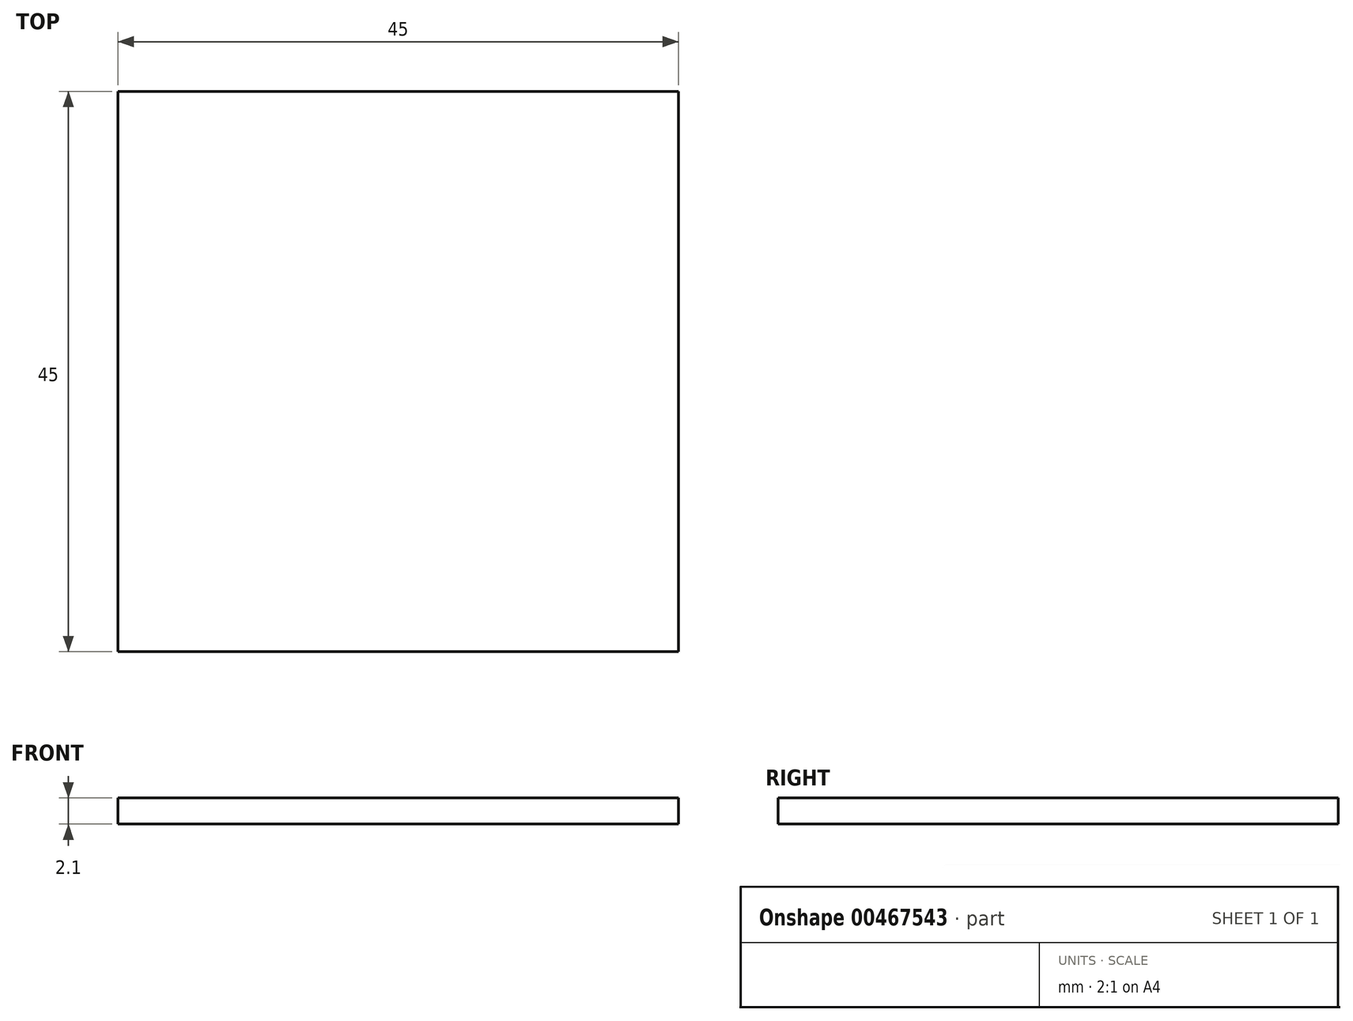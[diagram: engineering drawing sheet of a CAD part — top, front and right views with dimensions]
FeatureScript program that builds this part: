
annotation { "Feature Type Name" : "Feature", "Feature Type Description" : "" }
export const myFeature = defineFeature(function(context is Context, id is Id, definition is map)
    precondition{}
    {
        {
            var Q0;
            Q0=qCreatedBy(makeId("Top.planeOp"),FACE);
            var sketch = newSketch(context, id + "F0", { "sketchPlane" : qUnion([Q0])});
            skLineSegment(sketch, "E0.bottom", {"start": v(0, 0) * mm, "end": v(45, 0) * mm});
            skLineSegment(sketch, "E0.top", {"start": v(0, 45) * mm, "end": v(45, 45) * mm});
            skLineSegment(sketch, "E0.left", {"start": v(0, 0) * mm, "end": v(0, 45) * mm});
            skLineSegment(sketch, "E0.right", {"start": v(45, 0) * mm, "end": v(45, 45) * mm});
            skSolve(sketch);
        }
        {
            var Q0;
            Q0 = qSketchRegion(id + "F0", true);
            extrude(context, id + "F1", {"entities" : qUnion([Q0]), "depth" : 2.1 * mm});
        }
    });
